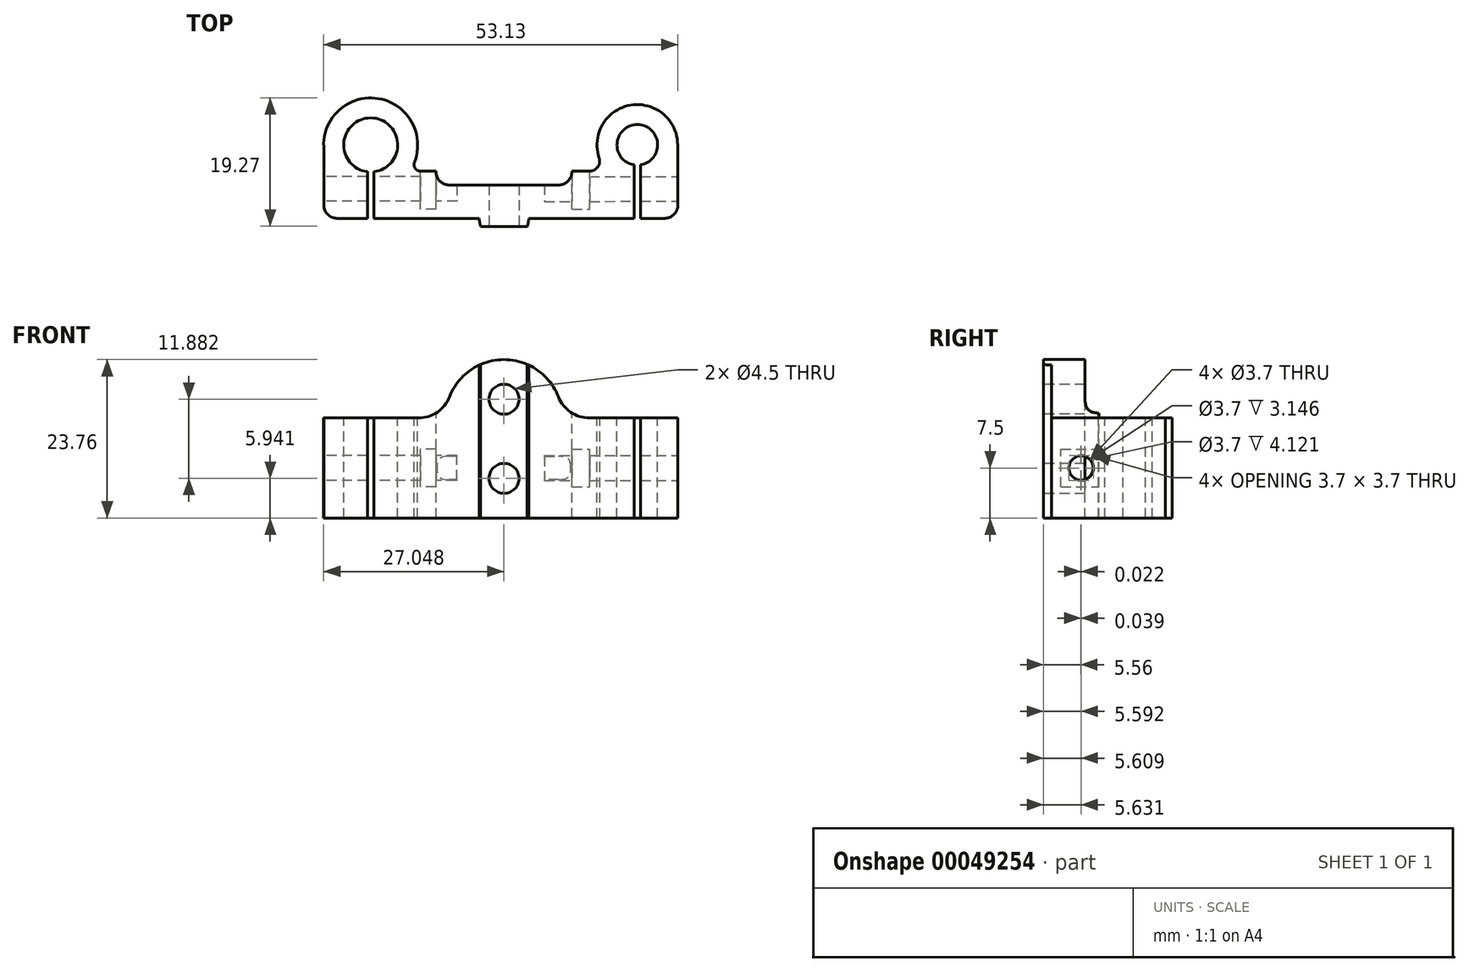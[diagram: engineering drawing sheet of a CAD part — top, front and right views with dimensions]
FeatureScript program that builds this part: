
annotation { "Feature Type Name" : "Feature", "Feature Type Description" : "" }
export const myFeature = defineFeature(function(context is Context, id is Id, definition is map)
    precondition{}
    {
        {
            var Q0;
            Q0=qCreatedBy(makeId("Top.planeOp"),FACE);
            var sketch = newSketch(context, id + "F0", { "sketchPlane" : qUnion([Q0])});
            skArc(sketch, "E0", {"start": v(12.6, -22.52) * mm, "mid": v(12.1, -16.46) * mm, "end": v(11.6, -22.52) * mm});
            skArc(sketch, "E1", {"start": v(-27.4, -23.53) * mm, "mid": v(-27.9, -15.46) * mm, "end": v(-28.4, -23.53) * mm});
            skArc(sketch, "E2", {"start": v(18.16, -19.49) * mm, "mid": v(11.1, -13.55) * mm, "end": v(6.38, -21.47) * mm});
            skArc(sketch, "E3", {"start": v(-21.33, -22.1) * mm, "mid": v(-26.72, -12.56) * mm, "end": v(-34.94, -19.8) * mm});
            skLineSegment(sketch, "E4", {"start": v(0.3, -25.53) * mm, "end": v(-16.08, -25.53) * mm});
            skLineSegment(sketch, "E5", {"start": v(-32.94, -30.53) * mm, "end": v(-28.4, -30.53) * mm});
            skLineSegment(sketch, "E6", {"start": v(-34.94, -19.8) * mm, "end": v(-34.94, -28.53) * mm});
            skPoint(sketch, "E7", {"position": v(-8.2, -30.53) * mm});
            skPoint(sketch, "E8", {"position": v(-8.2, -25.53) * mm});
            skLineSegment(sketch, "E9.rect.top", {"start": v(-27.4, -8.5) * mm, "end": v(-28.4, -8.5) * mm});
            skLineSegment(sketch, "E9.rect.left", {"start": v(-27.4, -30.53) * mm, "end": v(-27.4, -23.53) * mm});
            skLineSegment(sketch, "E9.rect.right", {"start": v(-28.4, -30.53) * mm, "end": v(-28.4, -23.53) * mm});
            skLineSegment(sketch, "E10.MirrorCS", {"start": v(-26.83, -5.34) * mm, "end": v(-27.83, -5.34) * mm});
            skLineSegment(sketch, "E11", {"start": v(-27.9, -19.51) * mm, "end": v(12.1, -19.51) * mm, "construction": true});
            skPoint(sketch, "E12", {"position": v(-7.9, -19.51) * mm});
            skLineSegment(sketch, "E13", {"start": v(-7.9, -19.51) * mm, "end": v(-7.9, -30.53) * mm, "construction": true});
            skLineSegment(sketch, "E14.MirrorCS", {"start": v(11.04, -5.34) * mm, "end": v(12.04, -5.34) * mm});
            skLineSegment(sketch, "E15.MirrorCS", {"start": v(12.6, -30.53) * mm, "end": v(12.6, -22.52) * mm});
            skLineSegment(sketch, "E16.MirrorCS", {"start": v(11.6, -30.53) * mm, "end": v(11.6, -22.52) * mm});
            skPoint(sketch, "E17.MirrorCS.end.orphan", {"position": v(12.6, -8.5) * mm});
            skPoint(sketch, "E18.orphan", {"position": v(11.6, -8.5) * mm});
            skPoint(sketch, "E19.MirrorCS.end.orphan", {"position": v(12.04, -5.34) * mm});
            skPoint(sketch, "E19.MirrorCS.start.orphan", {"position": v(11.04, -5.34) * mm});
            skLineSegment(sketch, "E20.trimOffspring", {"start": v(-27.4, -30.53) * mm, "end": v(-11.6, -30.53) * mm});
            skLineSegment(sketch, "E21.trimOffspring", {"start": v(12.6, -30.53) * mm, "end": v(16.2, -30.53) * mm});
            skLineSegment(sketch, "E22.filletArc", {"start": v(11.5, -25.53) * mm, "end": v(11.5, -25.53) * mm});
            skLineSegment(sketch, "E23.filletArc", {"start": v(-24.22, -25.53) * mm, "end": v(-24.22, -25.53) * mm});
            skPoint(sketch, "E24.orphan", {"position": v(18.12, -30.53) * mm});
            skLineSegment(sketch, "E25", {"start": v(18.2, -28.52) * mm, "end": v(18.16, -19.49) * mm});
            skPoint(sketch, "E26.orphan", {"position": v(-34.5, -30.53) * mm});
            skPoint(sketch, "E27.visualSharp", {"position": v(18.2, -30.53) * mm});
            skArc(sketch, "E27.filletArc", {"start": v(16.2, -30.53) * mm, "mid": v(17.61, -29.94) * mm, "end": v(18.2, -28.52) * mm});
            skPoint(sketch, "E28.visualSharp", {"position": v(-34.94, -30.53) * mm});
            skArc(sketch, "E28.filletArc", {"start": v(-34.94, -28.53) * mm, "mid": v(-34.35, -29.95) * mm, "end": v(-32.94, -30.53) * mm});
            skLineSegment(sketch, "E29.rect.bottom", {"start": v(-18.08, -28.96) * mm, "end": v(-20.58, -28.96) * mm});
            skLineSegment(sketch, "E29.rect.left", {"start": v(-18.08, -28.96) * mm, "end": v(-18.08, -25.53) * mm});
            skLineSegment(sketch, "E29.rect.right", {"start": v(-20.58, -28.96) * mm, "end": v(-20.58, -25.53) * mm});
            skPoint(sketch, "E29.rect.middle", {"position": v(-19.33, -26.2) * mm});
            skLineSegment(sketch, "E30.MirrorCS", {"start": v(4.8, -28.96) * mm, "end": v(4.8, -25.53) * mm});
            skLineSegment(sketch, "E31.MirrorCS", {"start": v(2.3, -28.96) * mm, "end": v(2.3, -25.53) * mm});
            skLineSegment(sketch, "E32.MirrorCS", {"start": v(2.3, -28.96) * mm, "end": v(4.8, -28.96) * mm});
            skPoint(sketch, "E33.MirrorP", {"position": v(3.55, -26.2) * mm});
            skPoint(sketch, "E34", {"position": v(-27.4, -27.03) * mm});
            skPoint(sketch, "E35.orphan", {"position": v(-20.58, -23.46) * mm});
            skPoint(sketch, "E36.orphan", {"position": v(-18.08, -23.46) * mm});
            skPoint(sketch, "E37.MirrorCS.end.orphan", {"position": v(4.8, -23.46) * mm});
            skPoint(sketch, "E37.MirrorCS.start.orphan", {"position": v(2.3, -23.46) * mm});
            skLineSegment(sketch, "E38", {"start": v(-20.58, -25.53) * mm, "end": v(-20.58, -23.46) * mm});
            skLineSegment(sketch, "E39", {"start": v(-18.08, -23.46) * mm, "end": v(-18.08, -23.53) * mm});
            skLineSegment(sketch, "E40", {"start": v(-20.4, -23.46) * mm, "end": v(-18.08, -23.46) * mm});
            skLineSegment(sketch, "E41", {"start": v(2.3, -23.46) * mm, "end": v(4.96, -23.46) * mm});
            skLineSegment(sketch, "E42", {"start": v(4.8, -25.53) * mm, "end": v(4.8, -23.46) * mm});
            skLineSegment(sketch, "E43", {"start": v(2.3, -23.46) * mm, "end": v(2.3, -23.53) * mm});
            skLineSegment(sketch, "E44.filletArc", {"start": v(-22.05, -23.46) * mm, "end": v(-22.05, -23.46) * mm});
            skLineSegment(sketch, "E45.filletArc", {"start": v(7.52, -23.46) * mm, "end": v(7.52, -23.46) * mm});
            skArc(sketch, "E46.filletArc", {"start": v(-21.33, -22.1) * mm, "mid": v(-21.23, -23.02) * mm, "end": v(-20.4, -23.46) * mm});
            skArc(sketch, "E47.filletArc", {"start": v(4.96, -23.46) * mm, "mid": v(6.18, -22.83) * mm, "end": v(6.38, -21.47) * mm});
            skArc(sketch, "E48.filletArc", {"start": v(-18.08, -23.53) * mm, "mid": v(-17.5, -24.95) * mm, "end": v(-16.08, -25.53) * mm});
            skArc(sketch, "E49.filletArc", {"start": v(0.3, -25.53) * mm, "mid": v(1.71, -24.95) * mm, "end": v(2.3, -23.53) * mm});
            skArc(sketch, "E50", {"start": v(-11.6, -30.53) * mm, "mid": v(-11.54, -31.14) * mm, "end": v(-11.4, -31.73) * mm});
            skLineSegment(sketch, "E51.trimOffspring", {"start": v(-4.2, -30.53) * mm, "end": v(11.6, -30.53) * mm});
            skLineSegment(sketch, "E52", {"start": v(-4.4, -31.73) * mm, "end": v(-11.4, -31.73) * mm});
            skArc(sketch, "E53.trimOffspring", {"start": v(-4.4, -31.73) * mm, "mid": v(-4.24, -31.14) * mm, "end": v(-4.2, -30.53) * mm});
            skSolve(sketch);
        }
        {
            var Q0;
            Q0 = qSketchRegion(id + "F0", true);
            var Q1;
            Q1=makeQuery(id+"F0.imprint","IMPRINT",FACE,{"disambiguationData":[TD([[makeQuery(id+"F0.imprint","IMPRINT",EDGE,{"derivedFrom":sQuery(id+"F0.wireOp",EDGE,"E0")}),-1.0]])]});
            extrude(context, id + "F1", {"entities" : qUnion([Q0, Q1]), "oppositeDirection" : true, "depth" : 15 * mm});
        }
        {
            var Q0;
            Q0=qCreatedBy(makeId("Right.planeOp"),FACE);
            var sketch = newSketch(context, id + "F2", { "sketchPlane" : qUnion([Q0])});
            skLineSegment(sketch, "E54.0.0", {"start": v(-19.49, 0) * mm, "end": v(-28.52, 0) * mm});
            skLineSegment(sketch, "E54.0.1", {"start": v(-28.52, 0) * mm, "end": v(-28.52, -15) * mm});
            skLineSegment(sketch, "E54.0.2", {"start": v(-28.52, -15) * mm, "end": v(-19.49, -15) * mm});
            skLineSegment(sketch, "E54.0.3", {"start": v(-19.49, -15) * mm, "end": v(-19.49, 0) * mm});
            skLineSegment(sketch, "E54.1.0", {"start": v(-28.52, 0) * mm, "end": v(-30.53, 0) * mm});
            skLineSegment(sketch, "E54.1.1", {"start": v(-30.53, 0) * mm, "end": v(-30.53, -15) * mm});
            skLineSegment(sketch, "E54.1.2", {"start": v(-30.53, -15) * mm, "end": v(-28.52, -15) * mm});
            skLineSegment(sketch, "E54.1.3", {"start": v(-28.52, -15) * mm, "end": v(-28.52, 0) * mm});
            skPoint(sketch, "E55", {"position": v(-19.49, -7.5) * mm});
            skLineSegment(sketch, "E56", {"start": v(-19.49, -7.5) * mm, "end": v(-30.53, -7.5) * mm});
            skPoint(sketch, "E57", {"position": v(-26.2, -7.5) * mm});
            skPoint(sketch, "E58", {"position": v(-29.45, -48.71) * mm});
            skPoint(sketch, "E59", {"position": v(-22.93, -48.71) * mm});
            skPoint(sketch, "E60.trimOffspring.end.orphan", {"position": v(-22.59, -47.18) * mm});
            skPoint(sketch, "E61.trimOffspring.start.orphan", {"position": v(-29.79, -47.18) * mm});
            skSolve(sketch);
        }
        {
            var Q0;
            Q0=makeQuery(id+"F1.opExtrude","SWEPT_FACE",FACE,{"disambiguationData":[OSD([sQuery(id+"F0.wireOp",EDGE,"E25")])]});
            var sketch = newSketch(context, id + "F3", { "sketchPlane" : qUnion([Q0])});
            skPoint(sketch, "E62", {"position": v(-28.96, -7.5) * mm});
            skPoint(sketch, "E63", {"position": v(-37.59, 27.7) * mm});
            skPoint(sketch, "E64", {"position": v(-31.07, 27.7) * mm});
            skPoint(sketch, "E65.trimOffspring.end.orphan", {"position": v(-30.73, 29.23) * mm});
            skPoint(sketch, "E66.start.orphan", {"position": v(-37.93, 29.23) * mm});
            skPoint(sketch, "E67", {"position": v(-23.46, -7.5) * mm});
            skLineSegment(sketch, "E68", {"start": v(-28.9, -7.5) * mm, "end": v(-28.96, -7.5) * mm});
            skLineSegment(sketch, "E69", {"start": v(-23.44, -7.5) * mm, "end": v(-23.46, -7.5) * mm});
            skPoint(sketch, "E70", {"position": v(-26.17, -7.5) * mm});
            skCircle(sketch, "E71", {"center": v(-26.17, -7.5) * mm, "radius": 1.85 * mm});
            skPoint(sketch, "E72.0.start.orphan", {"position": v(-19.49, -7.5) * mm});
            skPoint(sketch, "E73.orphan", {"position": v(-30.53, -7.5) * mm});
            skSolve(sketch);
        }
        {
            var Q0;
            Q0=makeQuery(id+"F1.opExtrude","SWEPT_FACE",FACE,{"disambiguationData":[OSD([sQuery(id+"F0.wireOp",EDGE,"E6")])]});
            var sketch = newSketch(context, id + "F4", { "sketchPlane" : qUnion([Q0])});
            skEllipse(sketch, "E74.0", {"center": v(26.1, -7.5) * mm, "majorRadius": 1.85 * mm, "minorRadius": 1.85 * mm, "majorAxis": v(0, 1)});
            skSolve(sketch);
        }
        {
            var Q0;
            Q0=makeQuery(id+"F4.imprint","IMPRINT",FACE,{"disambiguationData":[TD([[makeQuery(id+"F4.imprint","IMPRINT",EDGE,{"derivedFrom":sQuery(id+"F4.wireOp",EDGE,"E74.0")}),1.0]])]});
            extrude(context, id + "F5", {"entities" : qUnion([Q0]), "operationType" : NewBodyOperationType.REMOVE, "oppositeDirection" : true, "depth" : 20 * mm});
        }
        {
            var Q0;
            Q0 = qSketchRegion(id + "F3", true);
            var Q1;
            Q1=makeQuery(id+"F3.imprint","IMPRINT",FACE,{"disambiguationData":[TD([[makeQuery(id+"F3.imprint","IMPRINT",EDGE,{"derivedFrom":sQuery(id+"F3.wireOp",EDGE,"E71")}),1.0]])]});
            extrude(context, id + "F6", {"entities" : qUnion([Q0, Q1]), "operationType" : NewBodyOperationType.REMOVE, "oppositeDirection" : true, "depth" : 20 * mm});
        }
        {
            var Q0;
            Q0=makeQuery(id+"F1.opExtrude","SWEPT_FACE",FACE,{"disambiguationData":[OSD([sQuery(id+"F0.wireOp",EDGE,"E41")])]});
            var sketch = newSketch(context, id + "F7", { "sketchPlane" : qUnion([Q0])});
            skLineSegment(sketch, "E75", {"start": v(-2.3, -7.5) * mm, "end": v(-4.96, -7.5) * mm});
            skPoint(sketch, "E76", {"position": v(-3.63, -7.5) * mm});
            skLineSegment(sketch, "E77.rect.bottom", {"start": v(-2.3, -10.35) * mm, "end": v(-4.96, -10.35) * mm});
            skLineSegment(sketch, "E77.rect.top", {"start": v(-2.3, -4.65) * mm, "end": v(-4.96, -4.65) * mm});
            skLineSegment(sketch, "E77.rect.left", {"start": v(-2.3, -10.35) * mm, "end": v(-2.3, -4.65) * mm});
            skLineSegment(sketch, "E77.rect.right", {"start": v(-4.96, -10.35) * mm, "end": v(-4.96, -4.65) * mm});
            skLineSegment(sketch, "E78.0.0", {"start": v(20.4, 0) * mm, "end": v(18.08, 0) * mm});
            skLineSegment(sketch, "E78.0.1", {"start": v(18.08, 0) * mm, "end": v(18.08, -15) * mm});
            skLineSegment(sketch, "E78.0.2", {"start": v(18.08, -15) * mm, "end": v(20.4, -15) * mm});
            skLineSegment(sketch, "E78.0.3", {"start": v(20.4, -15) * mm, "end": v(20.4, 0) * mm});
            skLineSegment(sketch, "E79", {"start": v(-2.3, -7.5) * mm, "end": v(18.08, -7.5) * mm});
            skPoint(sketch, "E80", {"position": v(7.9, -7.5) * mm});
            skLineSegment(sketch, "E81", {"start": v(7.9, -7.5) * mm, "end": v(7.9, -15.38) * mm, "construction": true});
            skPoint(sketch, "E82.MirrorP", {"position": v(19.42, -7.5) * mm});
            skLineSegment(sketch, "E83.MirrorCS", {"start": v(18.08, -7.5) * mm, "end": v(20.75, -7.5) * mm});
            skLineSegment(sketch, "E84.MirrorCS", {"start": v(18.08, -10.35) * mm, "end": v(20.75, -10.35) * mm});
            skLineSegment(sketch, "E85.MirrorCS", {"start": v(18.08, -4.65) * mm, "end": v(20.75, -4.65) * mm});
            skLineSegment(sketch, "E86.MirrorCS", {"start": v(18.08, -10.35) * mm, "end": v(18.08, -4.65) * mm});
            skLineSegment(sketch, "E87.MirrorCS", {"start": v(18.08, -7.5) * mm, "end": v(-2.3, -7.5) * mm});
            skLineSegment(sketch, "E88.MirrorCS", {"start": v(20.75, -10.35) * mm, "end": v(20.75, -4.65) * mm});
            skSolve(sketch);
        }
        {
            var Q0;
            {var subQ0=sQuery(id+"F7.wireOp",EDGE,"E75");Q0=makeQuery(id+"F7.imprint","IMPRINT",FACE,{"disambiguationData":[TD([[makeQuery(id+"F7.imprint","IMPRINT",EDGE,{"derivedFrom":subQ0}),-1.0]])]});}
            var Q1;
            {var subQ0=sQuery(id+"F7.wireOp",EDGE,"E84.MirrorCS");var subQ1=sQuery(id+"F7.wireOp",EDGE,"E78.0.3");var subQ2=makeQuery(id+"F7.imprint","INTERSECT",VERTEX,{"derivedFrom":[subQ1,subQ0]});Q1=makeQuery(id+"F7.imprint","IMPRINT",FACE,{"disambiguationData":[TD([[makeQuery(id+"F7.imprint","IMPRINT",EDGE,{"disambiguationData":[TD([[subQ2,-1.0]])],"derivedFrom":subQ1}),1.0]])]});}
            var Q2;
            {var subQ0=sQuery(id+"F7.wireOp",EDGE,"E85.MirrorCS");var subQ1=sQuery(id+"F7.wireOp",EDGE,"E78.0.3");var subQ2=makeQuery(id+"F7.imprint","INTERSECT",VERTEX,{"derivedFrom":[subQ1,subQ0]});Q2=makeQuery(id+"F7.imprint","IMPRINT",FACE,{"disambiguationData":[TD([[makeQuery(id+"F7.imprint","IMPRINT",EDGE,{"disambiguationData":[TD([[subQ2,1.0]])],"derivedFrom":subQ1}),1.0]])]});}
            var Q3;
            {var subQ0=sQuery(id+"F7.wireOp",EDGE,"E75");Q3=makeQuery(id+"F7.imprint","IMPRINT",FACE,{"disambiguationData":[TD([[makeQuery(id+"F7.imprint","IMPRINT",EDGE,{"derivedFrom":subQ0}),1.0]])]});}
            extrude(context, id + "F8", {"entities" : qUnion([Q0, Q1, Q2, Q3]), "operationType" : NewBodyOperationType.REMOVE, "oppositeDirection" : true, "depth" : 5.7 * mm});
        }
        {
            var Q0;
            Q0=makeQuery(id+"F1.opExtrude","SWEPT_FACE",FACE,{"disambiguationData":[OSD([sQuery(id+"F0.wireOp",EDGE,"E20.trimOffspring")])]});
            var sketch = newSketch(context, id + "F9", { "sketchPlane" : qUnion([Q0])});
            skLineSegment(sketch, "E89.0.0", {"start": v(11.6, 0) * mm, "end": v(-4.2, 0) * mm});
            skLineSegment(sketch, "E89.0.1", {"start": v(-4.2, 0) * mm, "end": v(-4.2, -15) * mm});
            skLineSegment(sketch, "E89.0.2", {"start": v(-4.2, -15) * mm, "end": v(11.6, -15) * mm});
            skLineSegment(sketch, "E89.0.3", {"start": v(11.6, -15) * mm, "end": v(11.6, 0) * mm});
            skLineSegment(sketch, "E90", {"start": v(11.6, 0) * mm, "end": v(4.93, 0) * mm});
            skPoint(sketch, "E91", {"position": v(-7.9, 0) * mm});
            skArc(sketch, "E92", {"start": v(0.27, 3.18) * mm, "mid": v(-7.9, 8.76) * mm, "end": v(-16.06, 3.18) * mm});
            skLineSegment(sketch, "E93.trimOffspring", {"start": v(-20.72, 0) * mm, "end": v(-27.4, 0) * mm});
            skPoint(sketch, "E94.visualSharp", {"position": v(-16.66, 0) * mm});
            skArc(sketch, "E94.filletArc", {"start": v(-20.72, 0) * mm, "mid": v(-17.9, 0.87) * mm, "end": v(-16.06, 3.18) * mm});
            skPoint(sketch, "E95.visualSharp", {"position": v(0.87, 0) * mm});
            skArc(sketch, "E95.filletArc", {"start": v(0.27, 3.18) * mm, "mid": v(2.11, 0.87) * mm, "end": v(4.93, 0) * mm});
            skLineSegment(sketch, "E96", {"start": v(-20.72, 0) * mm, "end": v(4.93, 0) * mm});
            skSolve(sketch);
        }
        {
            var Q0;
            Q0=makeQuery(id+"F9.imprint","IMPRINT",FACE,{"disambiguationData":[TD([[makeQuery(id+"F9.imprint","IMPRINT",EDGE,{"derivedFrom":sQuery(id+"F9.wireOp",EDGE,"E92")}),1.0]])]});
            var Q1;
            Q1=makeQuery(id+"F1.opExtrude","SWEPT_FACE",FACE,{"disambiguationData":[OSD([sQuery(id+"F0.wireOp",EDGE,"E4")])]});
            extrude(context, id + "F10", {"entities" : qUnion([Q0]), "operationType" : NewBodyOperationType.ADD, "endBound" : BoundingType.UP_TO_SURFACE, "oppositeDirection" : true, "endBoundEntityFace" : qUnion([Q1]), "depth" : 25 * mm});
        }
        {
            var Q0;
            {var subQ0=sQuery(id+"F0.wireOp",EDGE,"E51.trimOffspring");var subQ1=sQuery(id+"F0.wireOp",EDGE,"E50");var subQ2=sQuery(id+"F0.wireOp",EDGE,"E52");var subQ3=sQuery(id+"F0.wireOp",EDGE,"E20.trimOffspring");var subQ4=sQuery(id+"F0.wireOp",EDGE,"E53.trimOffspring");Q0=makeQuery(id+"F10.boolean.opBoolean","SPLIT",FACE,{"disambiguationData":[TD([makeQuery(id+"F1.opExtrude","SWEPT_FACE",FACE,{"disambiguationData":[OSD([subQ1])]})])],"derivedFrom":makeQuery(id+"F1.opExtrude","CAP_FACE",FACE,{"disambiguationData":[OSD([sQuery(id+"F0.wireOp",EDGE,"E0"),sQuery(id+"F0.wireOp",EDGE,"E1"),sQuery(id+"F0.wireOp",EDGE,"E2"),sQuery(id+"F0.wireOp",EDGE,"E3"),sQuery(id+"F0.wireOp",EDGE,"E4"),sQuery(id+"F0.wireOp",EDGE,"E5"),sQuery(id+"F0.wireOp",EDGE,"E6"),sQuery(id+"F0.wireOp",EDGE,"E9.rect.left"),sQuery(id+"F0.wireOp",EDGE,"E9.rect.right"),sQuery(id+"F0.wireOp",EDGE,"E15.MirrorCS"),sQuery(id+"F0.wireOp",EDGE,"E16.MirrorCS"),subQ3,sQuery(id+"F0.wireOp",EDGE,"E21.trimOffspring"),sQuery(id+"F0.wireOp",EDGE,"E25"),sQuery(id+"F0.wireOp",EDGE,"E27.filletArc"),sQuery(id+"F0.wireOp",EDGE,"E28.filletArc"),sQuery(id+"F0.wireOp",EDGE,"E39"),sQuery(id+"F0.wireOp",EDGE,"E40"),sQuery(id+"F0.wireOp",EDGE,"E41"),sQuery(id+"F0.wireOp",EDGE,"E43"),sQuery(id+"F0.wireOp",EDGE,"E46.filletArc"),sQuery(id+"F0.wireOp",EDGE,"E47.filletArc"),sQuery(id+"F0.wireOp",EDGE,"E48.filletArc"),sQuery(id+"F0.wireOp",EDGE,"E49.filletArc"),subQ1,subQ0,subQ2,subQ4])],"isStart":true})});}
            var Q1;
            Q1=makeQuery(id+"F10.opExtrude","SWEPT_FACE",FACE,{"disambiguationData":[OSD([sQuery(id+"F9.wireOp",EDGE,"E92")])]});
            extrude(context, id + "F11", {"entities" : qUnion([Q0]), "operationType" : NewBodyOperationType.ADD, "endBound" : BoundingType.UP_TO_SURFACE, "endBoundEntityFace" : qUnion([Q1]), "depth" : 25 * mm});
        }
        {
            var Q0;
            {var subQ0=sQuery(id+"F0.wireOp",EDGE,"E52");Q0=makeQuery(id+"F11.boolean.opBoolean","MERGE",FACE,{"derivedFrom":[makeQuery(id+"F1.opExtrude","SWEPT_FACE",FACE,{"disambiguationData":[OSD([subQ0])]}),makeQuery(id+"F11.opExtrude","SWEPT_FACE",FACE,{"disambiguationData":[OSD([subQ0])]})]});}
            var sketch = newSketch(context, id + "F12", { "sketchPlane" : qUnion([Q0])});
            skLineSegment(sketch, "E97", {"start": v(-7.9, -15) * mm, "end": v(-7.9, -9.06) * mm});
            skPoint(sketch, "E98", {"position": v(-7.9, -3.12) * mm});
            skLineSegment(sketch, "E99", {"start": v(-7.9, -3.12) * mm, "end": v(-7.9, 2.82) * mm});
            skLineSegment(sketch, "E100", {"start": v(-7.9, 2.82) * mm, "end": v(-7.9, 8.76) * mm});
            skLineSegment(sketch, "E101", {"start": v(-7.9, -9.06) * mm, "end": v(-7.9, -3.12) * mm});
            skSolve(sketch);
        }
        {
            var Q0;
            Q0=sQuery(id+"F12.wireOp",VERTEX,"E100.start");
            var Q1;
            Q1=sQuery(id+"F12.wireOp",VERTEX,"E101.start");
            var Q2;
            Q2=makeQuery(id+"F1.opExtrude","SWEPT_BODY",BODY,{"disambiguationData":[OSD([sQuery(id+"F0.wireOp",EDGE,"E0"),sQuery(id+"F0.wireOp",EDGE,"E1"),sQuery(id+"F0.wireOp",EDGE,"E2"),sQuery(id+"F0.wireOp",EDGE,"E3"),sQuery(id+"F0.wireOp",EDGE,"E4"),sQuery(id+"F0.wireOp",EDGE,"E5"),sQuery(id+"F0.wireOp",EDGE,"E6"),sQuery(id+"F0.wireOp",EDGE,"E9.rect.left"),sQuery(id+"F0.wireOp",EDGE,"E9.rect.right"),sQuery(id+"F0.wireOp",EDGE,"E15.MirrorCS"),sQuery(id+"F0.wireOp",EDGE,"E16.MirrorCS"),sQuery(id+"F0.wireOp",EDGE,"E20.trimOffspring"),sQuery(id+"F0.wireOp",EDGE,"E21.trimOffspring"),sQuery(id+"F0.wireOp",EDGE,"E25"),sQuery(id+"F0.wireOp",EDGE,"E27.filletArc"),sQuery(id+"F0.wireOp",EDGE,"E28.filletArc"),sQuery(id+"F0.wireOp",EDGE,"E39"),sQuery(id+"F0.wireOp",EDGE,"E40"),sQuery(id+"F0.wireOp",EDGE,"E41"),sQuery(id+"F0.wireOp",EDGE,"E43"),sQuery(id+"F0.wireOp",EDGE,"E46.filletArc"),sQuery(id+"F0.wireOp",EDGE,"E47.filletArc"),sQuery(id+"F0.wireOp",EDGE,"E48.filletArc"),sQuery(id+"F0.wireOp",EDGE,"E49.filletArc"),sQuery(id+"F0.wireOp",EDGE,"E50"),sQuery(id+"F0.wireOp",EDGE,"E51.trimOffspring"),sQuery(id+"F0.wireOp",EDGE,"E52"),sQuery(id+"F0.wireOp",EDGE,"E53.trimOffspring")])]});
            hole(context, id + "F13", {"style" : HoleStyle.SIMPLE, "holeDiameter" : 4.5 * mm, "endStyle" : HoleEndStyle.THROUGH, "locations" : qUnion([Q0, Q1]), "scope" : qUnion([Q2])});
        }
        {
            var Q0;
            {var subQ0=sQuery(id+"F0.wireOp",EDGE,"E41");var subQ1=sQuery(id+"F0.wireOp",EDGE,"E20.trimOffspring");var subQ2=sQuery(id+"F0.wireOp",EDGE,"E25");var subQ3=sQuery(id+"F0.wireOp",EDGE,"E21.trimOffspring");var subQ4=sQuery(id+"F0.wireOp",EDGE,"E43");var subQ9=sQuery(id+"F0.wireOp",EDGE,"E16.MirrorCS");var subQ10=sQuery(id+"F0.wireOp",EDGE,"E0");var subQ11=sQuery(id+"F0.wireOp",EDGE,"E27.filletArc");var subQ12=sQuery(id+"F0.wireOp",EDGE,"E2");var subQ13=sQuery(id+"F0.wireOp",EDGE,"E4");var subQ14=sQuery(id+"F0.wireOp",EDGE,"E47.filletArc");var subQ15=sQuery(id+"F0.wireOp",EDGE,"E15.MirrorCS");var subQ16=sQuery(id+"F0.wireOp",EDGE,"E49.filletArc");var subQ17=sQuery(id+"F0.wireOp",EDGE,"E51.trimOffspring");Q0=makeQuery(id+"F10.boolean.opBoolean","SPLIT",FACE,{"disambiguationData":[TD([makeQuery(id+"F1.opExtrude","SWEPT_FACE",FACE,{"disambiguationData":[OSD([subQ10])]})])],"derivedFrom":makeQuery(id+"F1.opExtrude","CAP_FACE",FACE,{"disambiguationData":[OSD([subQ10,sQuery(id+"F0.wireOp",EDGE,"E1"),subQ12,sQuery(id+"F0.wireOp",EDGE,"E3"),subQ13,sQuery(id+"F0.wireOp",EDGE,"E5"),sQuery(id+"F0.wireOp",EDGE,"E6"),sQuery(id+"F0.wireOp",EDGE,"E9.rect.left"),sQuery(id+"F0.wireOp",EDGE,"E9.rect.right"),subQ15,subQ9,subQ1,subQ3,subQ2,subQ11,sQuery(id+"F0.wireOp",EDGE,"E28.filletArc"),sQuery(id+"F0.wireOp",EDGE,"E39"),sQuery(id+"F0.wireOp",EDGE,"E40"),subQ0,subQ4,sQuery(id+"F0.wireOp",EDGE,"E46.filletArc"),subQ14,sQuery(id+"F0.wireOp",EDGE,"E48.filletArc"),subQ16,sQuery(id+"F0.wireOp",EDGE,"E50"),subQ17,sQuery(id+"F0.wireOp",EDGE,"E52"),sQuery(id+"F0.wireOp",EDGE,"E53.trimOffspring")])],"isStart":true})});}
            var Q1;
            Q1=makeQuery(id+"F10.opExtrude","SWEPT_FACE",FACE,{"disambiguationData":[OSD([sQuery(id+"F9.wireOp",EDGE,"E95.filletArc")])]});
            extrude(context, id + "F14", {"entities" : qUnion([Q0]), "operationType" : NewBodyOperationType.ADD, "endBound" : BoundingType.UP_TO_SURFACE, "endBoundEntityFace" : qUnion([Q1]), "depth" : 25 * mm});
        }
        {
            var Q0;
            {var subQ0=sQuery(id+"F0.wireOp",EDGE,"E20.trimOffspring");var subQ1=sQuery(id+"F0.wireOp",EDGE,"E40");var subQ2=sQuery(id+"F0.wireOp",EDGE,"E28.filletArc");var subQ3=sQuery(id+"F0.wireOp",EDGE,"E9.rect.right");var subQ4=sQuery(id+"F0.wireOp",EDGE,"E51.trimOffspring");var subQ5=sQuery(id+"F0.wireOp",EDGE,"E9.rect.left");var subQ6=sQuery(id+"F0.wireOp",EDGE,"E6");var subQ8=sQuery(id+"F0.wireOp",EDGE,"E1");var subQ12=sQuery(id+"F0.wireOp",EDGE,"E3");var subQ13=sQuery(id+"F0.wireOp",EDGE,"E39");var subQ14=sQuery(id+"F0.wireOp",EDGE,"E4");var subQ15=sQuery(id+"F0.wireOp",EDGE,"E48.filletArc");var subQ16=sQuery(id+"F0.wireOp",EDGE,"E5");var subQ17=sQuery(id+"F0.wireOp",EDGE,"E46.filletArc");Q0=makeQuery(id+"F10.boolean.opBoolean","SPLIT",FACE,{"disambiguationData":[TD([makeQuery(id+"F1.opExtrude","SWEPT_FACE",FACE,{"disambiguationData":[OSD([subQ8])]})])],"derivedFrom":makeQuery(id+"F1.opExtrude","CAP_FACE",FACE,{"disambiguationData":[OSD([sQuery(id+"F0.wireOp",EDGE,"E0"),subQ8,sQuery(id+"F0.wireOp",EDGE,"E2"),subQ12,subQ14,subQ16,subQ6,subQ5,subQ3,sQuery(id+"F0.wireOp",EDGE,"E15.MirrorCS"),sQuery(id+"F0.wireOp",EDGE,"E16.MirrorCS"),subQ0,sQuery(id+"F0.wireOp",EDGE,"E21.trimOffspring"),sQuery(id+"F0.wireOp",EDGE,"E25"),sQuery(id+"F0.wireOp",EDGE,"E27.filletArc"),subQ2,subQ13,subQ1,sQuery(id+"F0.wireOp",EDGE,"E41"),sQuery(id+"F0.wireOp",EDGE,"E43"),subQ17,sQuery(id+"F0.wireOp",EDGE,"E47.filletArc"),subQ15,sQuery(id+"F0.wireOp",EDGE,"E49.filletArc"),sQuery(id+"F0.wireOp",EDGE,"E50"),subQ4,sQuery(id+"F0.wireOp",EDGE,"E52"),sQuery(id+"F0.wireOp",EDGE,"E53.trimOffspring")])],"isStart":true})});}
            var Q1;
            Q1=makeQuery(id+"F10.opExtrude","SWEPT_FACE",FACE,{"disambiguationData":[OSD([sQuery(id+"F9.wireOp",EDGE,"E94.filletArc")])]});
            extrude(context, id + "F15", {"entities" : qUnion([Q0]), "operationType" : NewBodyOperationType.ADD, "endBound" : BoundingType.UP_TO_SURFACE, "endBoundEntityFace" : qUnion([Q1]), "depth" : 25 * mm});
        }
    });
